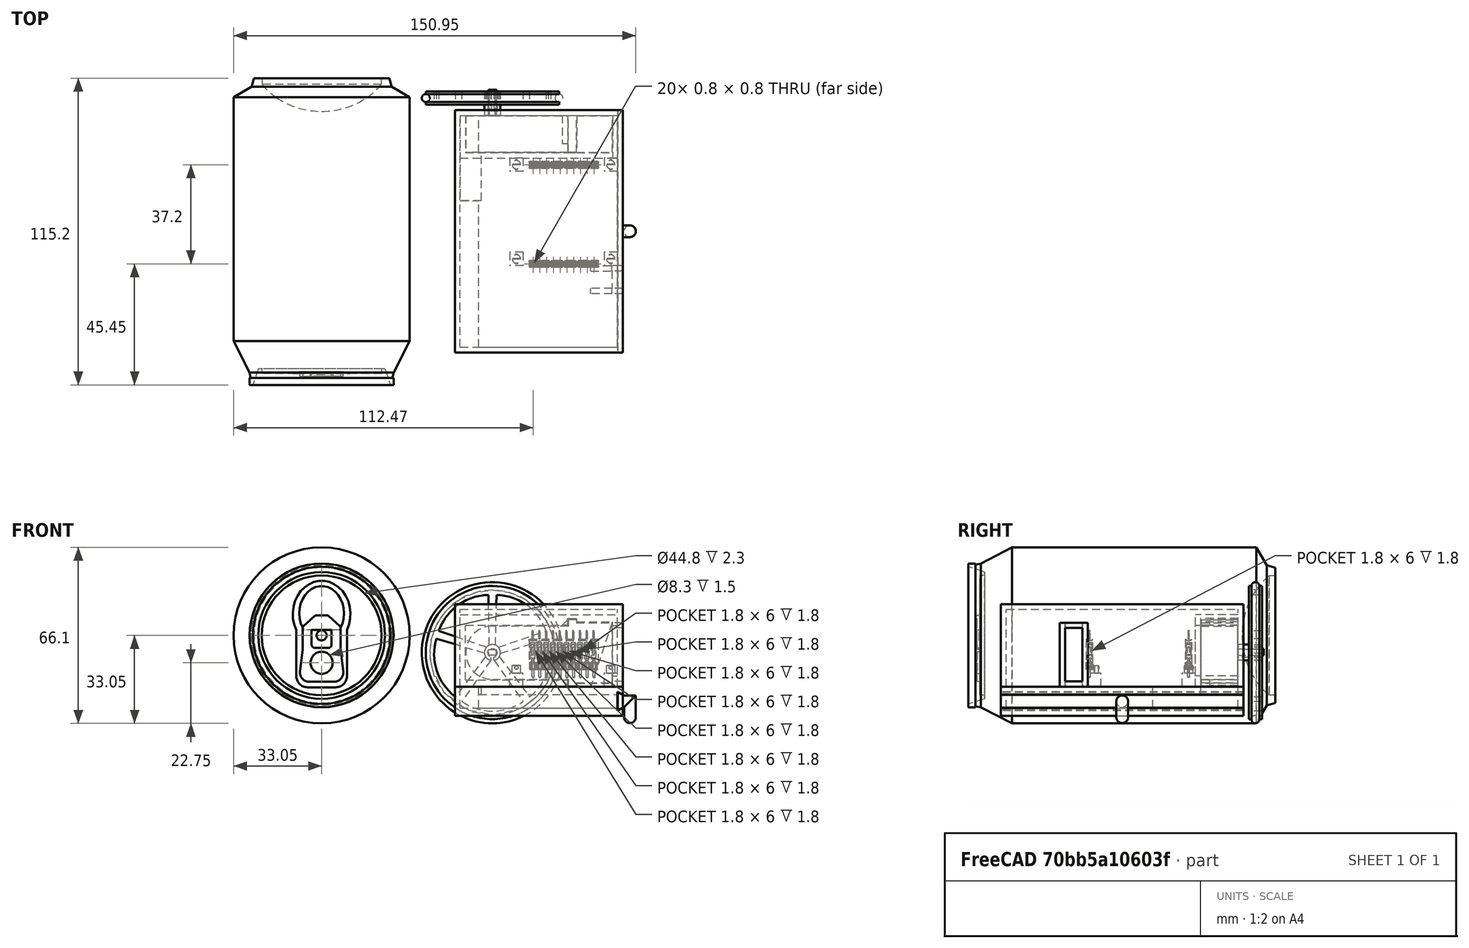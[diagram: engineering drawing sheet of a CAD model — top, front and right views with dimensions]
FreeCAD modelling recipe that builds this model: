
FCSTD DOCUMENT  (FreeCAD 0.16R6710 (Git))
Label: Rover
License: All rights reserved
LicenseURL: http://en.wikipedia.org/wiki/All_rights_reserved
objects: Part::Box×24, Part::Feature×23, Part::Cut×14, Part::MultiFuse×10, Part::Cylinder×8, Part::FeaturePython×7, Mesh::Feature×3, Part::Compound×3, Sketcher::SketchObject×3, App::DocumentObjectGroup×3, Part::Sphere×3, Part::Extrusion×3, PartDesign::Pad×2, Part::Torus×2, Part::Mirroring×1
note: 105 computed .brp shape members not serialized (recipe doc carries the construction recipe); baked Part::Feature solids carry a one-line shape summary decoded from their .brp

FEATURE [Mesh::Feature] neoBoard001  label="nanopi"
  Placement = pos=(15.42,13.25,2.65) rot=(0,0.707107,0.707107;3.14159rad)
FEATURE [Part::Feature] Part__Feature  label="Array002"
  shape: bbox 2.54 x 2.54 x 2.54 mm, 18 faces (baked)
FEATURE [Part::Feature] Part__Feature001  label="Array003"
  shape: bbox 2.54 x 2.54 x 2.54 mm, 18 faces (baked)
FEATURE [Part::Feature] Part__Feature002  label="Array004"
  shape: bbox 2.54 x 2.54 x 2.54 mm, 18 faces (baked)
FEATURE [Part::Feature] Part__Feature003  label="Array005"
  shape: bbox 2.54 x 2.54 x 2.54 mm, 18 faces (baked)
FEATURE [Part::Feature] Part__Feature004  label="Array006"
  shape: bbox 2.54 x 2.54 x 2.54 mm, 18 faces (baked)
FEATURE [Part::Feature] Part__Feature005  label="Array007"
  shape: bbox 2.54 x 2.54 x 2.54 mm, 18 faces (baked)
FEATURE [Part::Feature] Part__Feature006  label="Array008"
  shape: bbox 2.54 x 2.54 x 2.54 mm, 18 faces (baked)
FEATURE [Part::Feature] Part__Feature007  label="Array009"
  shape: bbox 2.54 x 2.54 x 2.54 mm, 18 faces (baked)
FEATURE [Part::Feature] Part__Feature008  label="Array010"
  shape: bbox 2.54 x 2.54 x 2.54 mm, 18 faces (baked)
FEATURE [Part::Feature] Part__Feature009  label="Array011"
  shape: bbox 2.54 x 2.54 x 2.54 mm, 18 faces (baked)
FEATURE [Part::Feature] Part__Feature010  label="Array012"
  shape: bbox 0.8 x 0.8 x 11.54 mm, 14 faces (baked)
FEATURE [Part::Feature] Part__Feature011  label="Array013"
  shape: bbox 0.8 x 0.8 x 11.54 mm, 14 faces (baked)
FEATURE [Part::Feature] Part__Feature012  label="Array014"
  shape: bbox 0.8 x 0.8 x 11.54 mm, 14 faces (baked)
FEATURE [Part::Feature] Part__Feature013  label="Array015"
  shape: bbox 0.8 x 0.8 x 11.54 mm, 14 faces (baked)
FEATURE [Part::Feature] Part__Feature014  label="Array016"
  shape: bbox 0.8 x 0.8 x 11.54 mm, 14 faces (baked)
FEATURE [Part::Feature] Part__Feature015  label="Array017"
  shape: bbox 0.8 x 0.8 x 11.54 mm, 14 faces (baked)
FEATURE [Part::Feature] Part__Feature016  label="Array018"
  shape: bbox 0.8 x 0.8 x 11.54 mm, 14 faces (baked)
FEATURE [Part::Feature] Part__Feature017  label="Array019"
  shape: bbox 0.8 x 0.8 x 11.54 mm, 14 faces (baked)
FEATURE [Part::Feature] Part__Feature018  label="Array020"
  shape: bbox 0.8 x 0.8 x 11.54 mm, 14 faces (baked)
FEATURE [Part::Feature] Part__Feature019  label="Array021"
  shape: bbox 0.8 x 0.8 x 11.54 mm, 14 faces (baked)
FEATURE [Part::Compound] Compound  label="1x10male"
  Links = -> [Part__Feature,Part__Feature001,Part__Feature008,Part__Feature017,Part__Feature018,Part__Feature019,Part__Feature010,Part__Feature009,Part__Feature011,Part__Feature003,Part__Feature004,Part__Feature005,Part__Feature007,Part__Feature006,Part__Feature002,Part__Feature012,Part__Feature013,Part__Feature014,Part__Feature016,Part__Feature015]
  Placement = pos=(11,-18.2,0) rot=(0,0,1;1.5708rad)
FEATURE [Part::Compound] Compound001  label="1x10male001"
  Links = -> [Part__Feature,Part__Feature001,Part__Feature008,Part__Feature017,Part__Feature018,Part__Feature019,Part__Feature010,Part__Feature009,Part__Feature011,Part__Feature003,Part__Feature004,Part__Feature005,Part__Feature007,Part__Feature006,Part__Feature002,Part__Feature012,Part__Feature013,Part__Feature014,Part__Feature016,Part__Feature015]
  Placement = pos=(11,19,0) rot=(0,0,1;1.5708rad)
FEATURE [Part::Feature] Part__Feature020  label="1x10female"
  Placement = pos=(-0.5,-18.2,7) rot=(-1,0,0;1.5708rad)
  shape: bbox 26 x 2.475 x 11.88 mm, 400 faces (baked)
FEATURE [Part::Feature] Part__Feature021  label="1x10female001"
  Placement = pos=(-0.5,19,7) rot=(-1,0,0;1.5708rad)
  shape: bbox 26 x 2.475 x 11.88 mm, 400 faces (baked)
FEATURE [Part::Compound] Compound002  label="headers"
  Links = -> [Compound,Part__Feature020,Part__Feature021,Compound001]
  Placement = pos=(15.42,13.25,3.45) rot=(0,0,1;3.14159rad)
FEATURE [Part::MultiFuse] Fusion  label="final-can"
  Placement = pos=(-75,64,16.25) rot=(1,0,0;1.5708rad)
FEATURE [Mesh::Feature] neoBoard2  label="neoBoardSMD"
  Placement = pos=(15.42,13.25,15.45) rot=(0,0.707107,0.707107;3.14159rad)
FEATURE [Mesh::Feature] neoBoard2001  label="neoBoardPCB"
  Placement = pos=(15.42,13.25,15.45) rot=(0,0.707107,0.707107;3.14159rad)
FEATURE [Sketcher::SketchObject] Sketch
  Placement = pos=(0,0,0) rot=(1,0,0;1.5708rad)
  sketch-geometry (12):
    g0: LineSegment StartX=-45 StartY=21.25 StartZ=0 EndX=-16.5 EndY=21.25 EndZ=0
    g1: LineSegment StartX=-16.5 StartY=21.25 StartZ=0 EndX=-16.5 EndY=23.65 EndZ=0
    g2: LineSegment StartX=-16.5 StartY=23.65 StartZ=0 EndX=-13.5 EndY=23.65 EndZ=0
    g3: LineSegment StartX=-13.5 StartY=-1.15 StartZ=0 EndX=-16.5 EndY=-1.15 EndZ=0
    g4: LineSegment StartX=-16.5 StartY=-1.15 StartZ=0 EndX=-16.5 EndY=1.25 EndZ=0
    g5: LineSegment StartX=-16.5 StartY=1.25 StartZ=0 EndX=-44.9999 EndY=1.25 EndZ=0
    g6: ArcOfCircle CenterX=-45 CenterY=11.25 CenterZ=0 NormalX=0 NormalY=0 NormalZ=1 Radius=10 StartAngle=1.5708 EndAngle=4.71239
    g7: LineSegment StartX=0 StartY=22.5 StartZ=0 EndX=0 EndY=0 EndZ=0
    g8: LineSegment StartX=-13.5 StartY=23.65 StartZ=0 EndX=-13.5 EndY=22.5 EndZ=0
    g9: LineSegment StartX=-13.5 StartY=22.5 StartZ=0 EndX=0 EndY=22.5 EndZ=0
    g10: LineSegment StartX=-13.5 StartY=-1.15 StartZ=0 EndX=-13.5 EndY=0 EndZ=0
    g11: LineSegment StartX=-13.5 StartY=0 StartZ=0 EndX=0 EndY=0 EndZ=0
  constraints (36):
    c: Horizontal(g0)
    c: Coincident(g0,g1)
    c: Vertical(g1)
    c: Coincident(g1,g2)
    c: Horizontal(g2)
    c: Horizontal(g3)
    c: Coincident(g3,g4)
    c: Vertical(g4)
    c: Coincident(g4,g5)
    c: Horizontal(g5)
    c: DistanceX(g2,g2) = 3
    c: DistanceY(g3,g2) = 24.8
    c: Equal(g2,g3)
    c: Equal(g1,g4)
    c: DistanceY(g4,g0) = 20
    c: Radius(g6) = 10
    c: DistanceY(g4,g6) = 10
    c: Coincident(g0,g6)
    c: Coincident(g5,g6)
    c: Vertical(g7)
    c: DistanceY(g7,g7) = 22.5
    c: Coincident(g2,g8)
    c: Vertical(g8)
    c: Coincident(g8,g9)
    c: Horizontal(g9)
    c: Coincident(g10,g3)
    c: Vertical(g10)
    c: Coincident(g11,g10)
    c: Horizontal(g11)
    c: Equal(g8,g10)
    c: Equal(g9,g11)
    c: Coincident(g9,g7)
    c: Coincident(g11,g7)
    c: DistanceX(g9,g9) = 13.5
    c: DistanceX(g0,g2) = 31.5
    c: Coincident(g7,g-1)
FEATURE [PartDesign::Pad] Pad  label="motorBody"
  Length = 13.8
  Length2 = 100
  Placement = pos=(0,0,0) rot=(1,0,0;1.5708rad)
  Sketch = -> Sketch
  Type = 0
FEATURE [Part::Box] Box001  label="batteryHole"
  Height = 5
  Length = 54
  Placement = pos=(-16,-37,-11) rot=(0,0,1;0rad)
  Width = 87
FEATURE [Part::Cylinder] Cylinder
  Angle = 360
  Height = 5
  Radius = 25
FEATURE [Part::Torus] Torus
  Angle1 = -180
  Angle2 = 180
  Angle3 = 360
  Placement = pos=(0,0,2.5) rot=(0,0,1;0rad)
  Radius1 = 25
  Radius2 = 1.5
FEATURE [Part::Cut] Cut001  label="wheel-base"
  Base = -> Cylinder
  Tool = -> Torus
FEATURE [Part::Cylinder] Cylinder001
  Angle = 360
  Height = 9.7
  Placement = pos=(-45,-13.8,11.25) rot=(1,0,0;1.5708rad)
  Radius = 1.5
FEATURE [Part::Box] Box002  label="Cube001"
  Height = 3
  Length = 3
  Placement = pos=(-46.5,-23.7,12.25) rot=(0,0,1;0rad)
  Width = 10
FEATURE [Part::Cut] Cut  label="motorShaft"
  Base = -> Cylinder001
  Tool = -> Box002
FEATURE [Part::MultiFuse] Fusion001  label="motor"
  Placement = pos=(34.1,-23.1,-1.5) rot=(0,0,1;0rad)
  Shapes = -> [Cut,Pad]
FEATURE [Part::Cylinder] Cylinder002
  Angle = 360
  Height = 9
  Radius = 1.8
FEATURE [Part::Box] Box003  label="Cube002"
  Height = 10
  Length = 10
  Placement = pos=(-3,1.1,0) rot=(0,0,1;0rad)
  Width = 10
FEATURE [Part::Cut] Cut002  label="shaftHole"
  Base = -> Cylinder002
  Tool = -> Box003
FEATURE [App::DocumentObjectGroup] Group  label="PCB"
  Group = -> [Compound002,neoBoard2,neoBoard2001,neoBoard001]
FEATURE [Part::Torus] Torus001
  Angle1 = -180
  Angle2 = 180
  Angle3 = 360
  Placement = pos=(-10.9,-43.5,9.75) rot=(1,0,0;1.5708rad)
  Radius1 = 25
  Radius2 = 1.5
FEATURE [Part::Box] Box004  label="Cube"
  Height = 11
  Length = 63
  Placement = pos=(-25,-39,-14) rot=(0,0,1;0rad)
  Width = 91
FEATURE [Part::FeaturePython] Clone  label="Clone of motor"  # Draft clone (typed FeaturePython)
  Objects = -> [Fusion001]
  Placement = pos=(34.1,36.1,21) rot=(1,0,0;3.14159rad)
  Scale = (1,1,1)
FEATURE [Part::FeaturePython] Clone002  label="Clone of Torus001"  # Draft clone (typed FeaturePython)
  Objects = -> [Torus001]
  Placement = pos=(-10.9,56.5,9.75) rot=(1,0,0;1.5708rad)
  Scale = (1,1,1)
FEATURE [Part::Cut] Cut004
  Base = -> Box004
  Tool = -> Box001
FEATURE [Part::Box] Box  label="Cube003"
  Height = 2.5
  Length = 38.34
  Placement = pos=(-20.1,-37,-3) rot=(0,0,1;0rad)
  Width = 14
FEATURE [Part::Box] Box005  label="Cube004"
  Height = 1.2
  Length = 13.4
  Placement = pos=(21.7,-37,-3) rot=(0,0,1;0rad)
  Width = 14
FEATURE [Part::Box] Box007  label="Cube006"
  Height = 27
  Length = 55.2
  Placement = pos=(-20.1,-23,-3) rot=(0,0,1;0rad)
  Width = 2
FEATURE [Part::Box] Box008  label="Cube007"
  Height = 27
  Length = 2
  Placement = pos=(-22.1,-37,-3) rot=(0,0,1;0rad)
  Width = 16
FEATURE [Part::Box] Box009  label="Cube008"
  Height = 4
  Length = 1.8
  Placement = pos=(35.1,-37,-3) rot=(0,0,1;0rad)
  Width = 16
FEATURE [Sketcher::SketchObject] Sketch001  label="SketchConnectorHole"
  Placement = pos=(46.6,52,-18.45) rot=(0,0.707107,-0.707107;3.14159rad)
  sketch-geometry (4):
    g0: LineSegment StartX=10.5462 StartY=-6.44881 StartZ=0 EndX=10.5462 EndY=-13.4488 EndZ=0
    g1: LineSegment StartX=10.5462 StartY=-13.4488 StartZ=0 EndX=8.54624 EndY=-12.4488 EndZ=0
    g2: LineSegment StartX=8.54624 StartY=-12.4488 StartZ=0 EndX=8.54624 EndY=-7.44881 EndZ=0
    g3: LineSegment StartX=8.54624 StartY=-7.44881 StartZ=0 EndX=10.5462 EndY=-6.44881 EndZ=0
  constraints (10):
    c: Vertical(g0)
    c: Coincident(g0,g1)
    c: Coincident(g1,g2)
    c: Vertical(g2)
    c: Coincident(g2,g3)
    c: Coincident(g3,g0)
    c: DistanceY(g0,g0) = 7
    c: DistanceY(g2,g2) = 5
    c: DistanceX(g2,g0) = 2
    c: Equal(g3,g1)
FEATURE [Part::Box] Box012  label="Cube011"
  Height = 31
  Length = 63
  Placement = pos=(-25,-41,-3) rot=(0,0,1;0rad)
  Width = 91
FEATURE [Part::Box] Box013  label="Cube012"
  Height = 29
  Length = 59
  Placement = pos=(-23,-39,-3) rot=(0,0,1;0rad)
  Width = 87
FEATURE [Part::Cut] Cut009
  Base = -> Box012
  Placement = pos=(0,2,0) rot=(0,0,1;0rad)
  Tool = -> Box013
FEATURE [Part::Cylinder] Cylinder004
  Angle = 360
  Height = 3
  Placement = pos=(0,0,2) rot=(0,0,1;0rad)
  Radius = 1.57
FEATURE [Part::Box] Box016  label="Cube015"
  Height = 5
  Length = 5
  Placement = pos=(-2.5,-2.5,-3) rot=(0,0,1;0rad)
  Width = 5
FEATURE [Part::Box] Box017  label="Cube016"
  Height = 3
  Length = 5
  Placement = pos=(-2.5,-0.125,2) rot=(0,0,1;0rad)
  Width = 0.25
FEATURE [Part::Cut] Cut011
  Base = -> Cylinder004
  Tool = -> Box017
FEATURE [Part::Sphere] Sphere
  Angle1 = -90
  Angle2 = 90
  Angle3 = 360
  Placement = pos=(0,1,4.1) rot=(0,0,1;0rad)
  Radius = 0.8
FEATURE [Part::Sphere] Sphere001
  Angle1 = -90
  Angle2 = 90
  Angle3 = 360
  Placement = pos=(0,-1,4.1) rot=(0,0,1;0rad)
  Radius = 0.8
FEATURE [Part::MultiFuse] Fusion006
  Shapes = -> [Box016,Sphere,Sphere001,Cut011]
FEATURE [Part::FeaturePython] Array001  label="PCBholder"  # Draft array (typed FeaturePython)
  Angle = 360
  ArrayType = 0
  Axis = (0,0,1)
  Base = -> Fusion006
  Center = (0,0,0)
  Fuse = false
  IntervalAxis = (0,0,0)
  IntervalX = (35.4,0,0)
  IntervalY = (0,35.4,0)
  IntervalZ = (0,0,0)
  NumberPolar = 1
  NumberX = 2
  NumberY = 2
  NumberZ = 1
  Placement = pos=(33.5,31.5,0) rot=(0,0,1;3.14159rad)
FEATURE [Part::Box] Box018  label="Cube017"
  Height = 2.5
  Length = 38.34
  Placement = pos=(-20.1,-37,20.1) rot=(0,0,1;0rad)
  Width = 14
FEATURE [Part::Box] Box019  label="Cube018"
  Height = 1.2
  Length = 13.4
  Placement = pos=(21.7,-37,21.4) rot=(0,0,1;0rad)
  Width = 14
FEATURE [Part::Box] Box020  label="Cube019"
  Height = 1.4
  Length = 55.2
  Placement = pos=(-20.1,-37,22.6) rot=(0,0,1;0rad)
  Width = 14
FEATURE [Part::Box] Box021  label="Cube020"
  Height = 4
  Length = 1.8
  Placement = pos=(35.1,-37,20) rot=(0,0,1;0rad)
  Width = 16
FEATURE [Part::MultiFuse] Fusion007  label="Fusion"
  Placement = pos=(-0.9,0,0) rot=(0,0,1;0rad)
  Shapes = -> [Box005,Box021,Box,Box007,Box008,Box009,Box019,Box018,Box020]
FEATURE [PartDesign::Pad] Pad001  label="batterySliderHole"
  Length = 91
  Length2 = 100
  Placement = pos=(46.6,52,-18.45) rot=(0,0.707107,-0.707107;3.14159rad)
  Sketch = -> Sketch001
  Type = 0
FEATURE [Part::FeaturePython] Clone004  label="batterySlider"  # Draft clone (typed FeaturePython)
  Objects = -> [Pad001]
  Placement = pos=(49.58,52,-18.85) rot=(0,0.707107,-0.707107;3.14159rad)
  Scale = (0.92,1,0.95)
FEATURE [Part::Cut] Cut012
  Base = -> Cut004
  Tool = -> Pad001
FEATURE [Part::Box] Box022  label="Cube022"
  Height = 8
  Length = 7
  Placement = pos=(-23,36,-11) rot=(0,0,1;0rad)
  Width = 14
FEATURE [Part::Box] Box023  label="Cube021"
  Height = 9
  Length = 8
  Placement = pos=(-23,18,-11) rot=(0,0,1;0rad)
  Width = 18
FEATURE [Part::MultiFuse] Fusion008  label="batteryCableHole"
  Shapes = -> [Box022,Box023]
FEATURE [Part::Cut] Cut013
  Base = -> Cut012
  Tool = -> Fusion008
FEATURE [Part::Box] Box024  label="Cube023"
  Height = 24
  Length = 4
  Placement = pos=(38,-8,-3) rot=(0,0,1;3.14159rad)
  Width = 10.5
FEATURE [Part::Box] Box025  label="Cube024"
  Height = 20
  Length = 4
  Placement = pos=(38,-10,-1) rot=(0,0,1;3.14159rad)
  Width = 6.5
FEATURE [Part::Cut] Cut014
  Base = -> Box024
  Tool = -> Box025
FEATURE [Part::Sphere] Sphere002
  Angle1 = -90
  Angle2 = 0
  Angle3 = 360
  Placement = pos=(40.7,6.5,-14.5) rot=(0,0,1;0rad)
  Radius = 2.2
FEATURE [Part::Cylinder] Cylinder006
  Angle = 360
  Height = 6
  Placement = pos=(43.9,6.5,-8.5) rot=(0,-1,0;1.5708rad)
  Radius = 2.2
FEATURE [Part::Box] Box026  label="Cube025"
  Height = 9
  Length = 5
  Placement = pos=(38.7,4,-11.5) rot=(0,1,0;0.785398rad)
  Width = 5
FEATURE [Part::Cut] Cut015
  Base = -> Cylinder006
  Placement = pos=(-1,0,0) rot=(0,0,1;0rad)
  Tool = -> Box026
FEATURE [Part::Cylinder] Cylinder007
  Angle = 360
  Height = 8.2
  Placement = pos=(43.9,6.5,-8.5) rot=(0,-1,0;1.5708rad)
  Radius = 2.2
FEATURE [Part::Box] Box027  label="Cube026"
  Height = 9
  Length = 5
  Placement = pos=(38.7,4,-11.5) rot=(0,1,0;0.785398rad)
  Width = 5
FEATURE [Part::Cut] Cut016
  Base = -> Cylinder007
  Placement = pos=(49.2,13,-50.2) rot=(0.707107,0,0.707107;3.14159rad)
  Tool = -> Box027
FEATURE [Part::MultiFuse] Fusion010
  Shapes = -> [Cut015,Cut016,Sphere002]
FEATURE [Part::FeaturePython] Clone005  label="batterySlider001"  # Draft clone (typed FeaturePython)
  Objects = -> [Pad001]
  Placement = pos=(49.58,52,-18.85) rot=(0,0.707107,-0.707107;3.14159rad)
  Scale = (0.92,1,0.95)
FEATURE [Part::MultiFuse] Fusion011  label="batterySliderLeg"
  Shapes = -> [Fusion010,Clone005]
FEATURE [Sketcher::SketchObject] Sketch002
  ExternalGeometry = -> [Fusion007]
  Placement = pos=(-0.9,-37,0) rot=(1,0,0;1.5708rad)
  Support = -> Fusion007 [Face20]
  sketch-geometry (6):
    g0: LineSegment StartX=16.24 StartY=-0.5 StartZ=0 EndX=18.24 EndY=-0.5 EndZ=0
    g1: LineSegment StartX=18.24 StartY=-0.5 StartZ=0 EndX=18.24 EndY=-2.5 EndZ=0
    g2: LineSegment StartX=18.24 StartY=-2.5 StartZ=0 EndX=16.24 EndY=-0.5 EndZ=0
    g3: LineSegment StartX=18.24 StartY=22.1 StartZ=0 EndX=18.24 EndY=20.1 EndZ=0
    g4: LineSegment StartX=18.24 StartY=20.1 StartZ=0 EndX=16.24 EndY=20.1 EndZ=0
    g5: LineSegment StartX=16.24 StartY=20.1 StartZ=0 EndX=18.24 EndY=22.1 EndZ=0
  constraints (16):
    c: Horizontal(g0)
    c: Coincident(g0,g1)
    c: Vertical(g1)
    c: Coincident(g1,g2)
    c: Coincident(g2,g0)
    c: DistanceY(g1,g1) = 2
    c: DistanceX(g0,g0) = 2
    c: Coincident(g-4,g0)
    c: Vertical(g3)
    c: Coincident(g3,g4)
    c: Horizontal(g4)
    c: Coincident(g4,g5)
    c: Coincident(g5,g3)
    c: DistanceY(g3,g3) = 2
    c: DistanceX(g4,g4) = 2
    c: Coincident(g3,g-6)
FEATURE [Part::Extrusion] Extrude  label="motorClipHoles"
  Base = -> Sketch002
  Dir = (0,10.7,0)
  Solid = true
FEATURE [Part::Cut] Cut017  label="motorHolder"
  Base = -> Fusion007
  Tool = -> Extrude
FEATURE [App::DocumentObjectGroup] Group002  label="BatteryLid"
  Group = -> [Clone004,Fusion011]
FEATURE [Part::Feature] Face
  shape: bbox 8.033 x 2e-07 x 24.13 mm, 1 faces, 0 solids (baked)
FEATURE [Part::Extrusion] Extrude001
  Base = -> Face
  Dir = (0,2,0)
  Placement = pos=(0,8.5,0) rot=(0,0,1;0rad)
  Solid = true
FEATURE [Part::Extrusion] Extrude002
  Base = -> Face
  Dir = (0,2,0)
  Solid = true
FEATURE [Part::MultiFuse] Fusion012  label="switchHolder"
  Placement = pos=(0,1.6,0) rot=(0,0,1;0rad)
  Shapes = -> [Cut014,Extrude002,Extrude001]
FEATURE [Part::Mirroring] mirror  label="Mirror of motorHolder"
  Base = (-23,-21,0)
  Normal = (0,-1,0)
  Placement = pos=(0,55,0) rot=(0,0,1;0rad)
  Source = -> Cut017
FEATURE [Part::Cylinder] Cylinder010
  Angle = 360
  Height = 9
  Radius = 3
FEATURE [Part::Box] Box030  label="Cube029"
  Height = 9
  Length = 1
  Placement = pos=(-0.5,-3.5,0) rot=(0,0,1;0rad)
  Width = 2
FEATURE [Part::MultiFuse] Fusion015
  Shapes = -> [Box030,Cut002]
FEATURE [Part::Cylinder] Cylinder012
  Angle = 70
  Height = 10
  Placement = pos=(0,-2,0) rot=(0,0,1;4.10152rad)
  Radius = 20
FEATURE [Part::FeaturePython] Array  label="Array022"  # Draft array (typed FeaturePython)
  Angle = 360
  ArrayType = 1
  Axis = (0,0,1)
  Base = -> Cylinder012
  Center = (0,0,0)
  Fuse = false
  IntervalAxis = (0,0,0)
  IntervalX = (1,0,0)
  IntervalY = (0,1,0)
  IntervalZ = (0,0,0)
  NumberPolar = 5
  NumberX = 2
  NumberY = 2
  NumberZ = 1
FEATURE [Part::Cut] Cut023
  Base = -> Cut001
  Tool = -> Array
FEATURE [Part::MultiFuse] Fusion016
  Shapes = -> [Cut023,Cylinder010]
FEATURE [Part::Cut] Cut024  label="wheel"
  Base = -> Fusion016
  Placement = pos=(-10.9,-46,9.8) rot=(0,0.707107,0.707107;3.14159rad)
  Tool = -> Fusion015
FEATURE [Part::FeaturePython] Clone006  label="Clone of wheel"  # Draft clone (typed FeaturePython)
  Objects = -> [Cut024]
  Placement = pos=(-10.9,59,9.8) rot=(1,0,0;1.5708rad)
  Scale = (1,1,1)
FEATURE [App::DocumentObjectGroup] Group001  label="Extras"
  Group = -> [Torus001,Fusion,Clone,Clone002,Group,Clone006]
